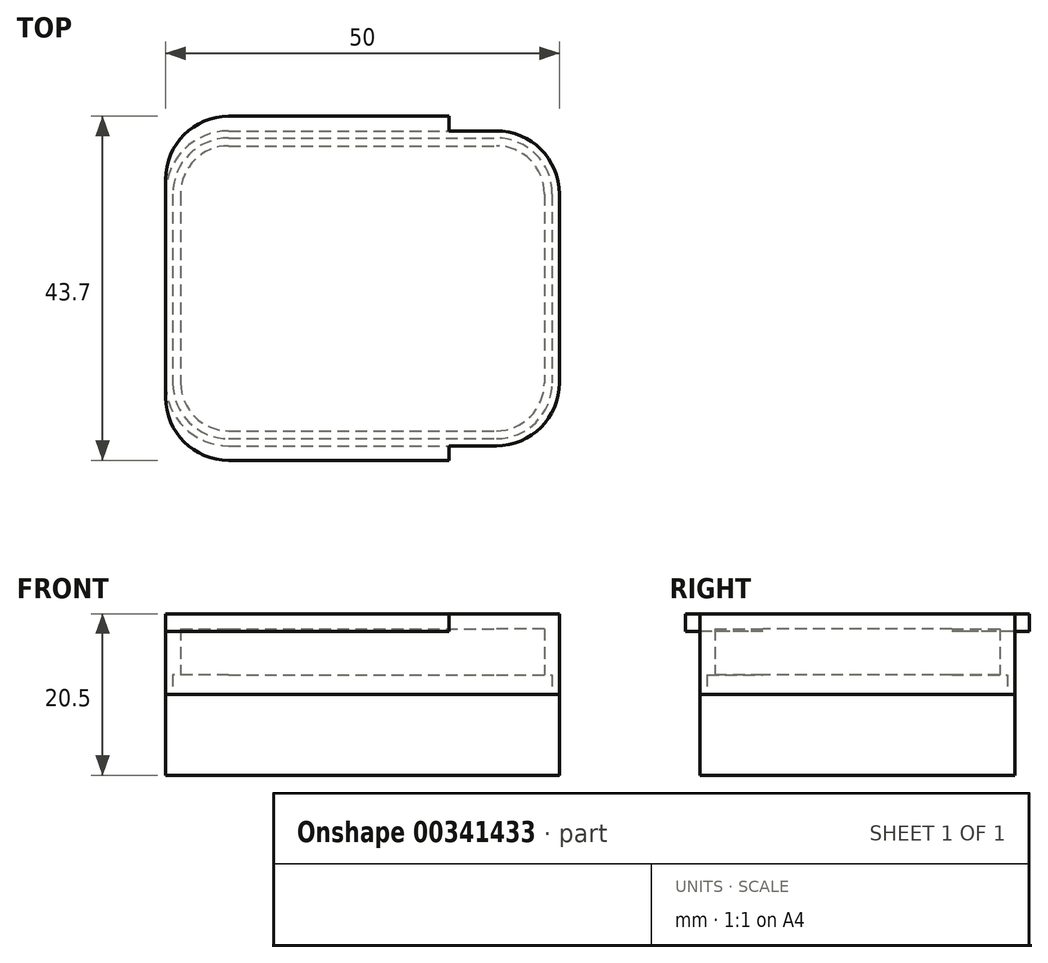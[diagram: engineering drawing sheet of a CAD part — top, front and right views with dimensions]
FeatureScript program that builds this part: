
annotation { "Feature Type Name" : "Feature", "Feature Type Description" : "" }
export const myFeature = defineFeature(function(context is Context, id is Id, definition is map)
    precondition{}
    {
        {
            var Q0;
            Q0=qCreatedBy(makeId("Top.planeOp"),FACE);
            var sketch = newSketch(context, id + "F0", { "sketchPlane" : qUnion([Q0])});
            skLineSegment(sketch, "E0.bottom", {"start": v(-17, 20) * mm, "end": v(17, 20) * mm});
            skLineSegment(sketch, "E0.top", {"start": v(-17, -20) * mm, "end": v(17, -20) * mm});
            skLineSegment(sketch, "E0.left", {"start": v(-25, 12) * mm, "end": v(-25, -12) * mm});
            skLineSegment(sketch, "E0.right", {"start": v(25, 12) * mm, "end": v(25, -12) * mm});
            skPoint(sketch, "E1.visualSharp", {"position": v(25, 20) * mm});
            skArc(sketch, "E1.filletArc", {"start": v(25, 12) * mm, "mid": v(22.66, 17.66) * mm, "end": v(17, 20) * mm});
            skPoint(sketch, "E2.visualSharp", {"position": v(-25, 20) * mm});
            skPoint(sketch, "E3.visualSharp", {"position": v(-25, -20) * mm});
            skArc(sketch, "E3.filletArc", {"start": v(-25, -12) * mm, "mid": v(-22.66, -17.66) * mm, "end": v(-17, -20) * mm});
            skPoint(sketch, "E4.visualSharp", {"position": v(25, -20) * mm});
            skArc(sketch, "E5.filletArc", {"start": v(-17, 20) * mm, "mid": v(-22.66, 17.66) * mm, "end": v(-25, 12) * mm});
            skArc(sketch, "E6.filletArc", {"start": v(17, -20) * mm, "mid": v(22.66, -17.66) * mm, "end": v(25, -12) * mm});
            skSolve(sketch);
        }
        {
            var Q0;
            Q0=makeQuery(id+"F0.imprint","IMPRINT",FACE,{"disambiguationData":[TD([[makeQuery(id+"F0.imprint","IMPRINT",EDGE,{"derivedFrom":sQuery(id+"F0.wireOp",EDGE,"E0.bottom")}),-1.0]])]});
            extrude(context, id + "F1", {"entities" : qUnion([Q0]), "depth" : 10.25 * mm});
        }
        {
            var Q0;
            Q0=makeQuery(id+"F1.opExtrude","CAP_FACE",FACE,{"disambiguationData":[OSD([sQuery(id+"F0.wireOp",EDGE,"E0.bottom"),sQuery(id+"F0.wireOp",EDGE,"E0.top"),sQuery(id+"F0.wireOp",EDGE,"E0.left"),sQuery(id+"F0.wireOp",EDGE,"E0.right"),sQuery(id+"F0.wireOp",EDGE,"E1.filletArc"),sQuery(id+"F0.wireOp",EDGE,"E3.filletArc"),sQuery(id+"F0.wireOp",EDGE,"E5.filletArc"),sQuery(id+"F0.wireOp",EDGE,"E6.filletArc")])],"isStart":false});
            var sketch = newSketch(context, id + "F2", { "sketchPlane" : qUnion([Q0])});
            skLineSegment(sketch, "E7.bottom", {"start": v(-17, 21.85) * mm, "end": v(11, 21.85) * mm});
            skLineSegment(sketch, "E7.top", {"start": v(-17, -21.85) * mm, "end": v(11, -21.85) * mm});
            skLineSegment(sketch, "E7.left", {"start": v(-25, 13.85) * mm, "end": v(-25, -13.85) * mm});
            skLineSegment(sketch, "E7.right", {"start": v(11, 21.85) * mm, "end": v(11, -21.85) * mm});
            skPoint(sketch, "E8.visualSharp", {"position": v(-25, 21.85) * mm});
            skArc(sketch, "E8.filletArc", {"start": v(-17, 21.85) * mm, "mid": v(-22.66, 19.5) * mm, "end": v(-25, 13.85) * mm});
            skPoint(sketch, "E9.visualSharp", {"position": v(-25, -21.85) * mm});
            skArc(sketch, "E9.filletArc", {"start": v(-25, -13.85) * mm, "mid": v(-22.66, -19.5) * mm, "end": v(-17, -21.85) * mm});
            skSolve(sketch);
        }
        {
            var Q0;
            {var subQ4=sQuery(id+"F2.wireOp",EDGE,"E7.bottom");Q0=makeQuery(id+"F2.imprint","IMPRINT",FACE,{"disambiguationData":[TD([[makeQuery(id+"F2.imprint","IMPRINT",EDGE,{"derivedFrom":subQ4}),-1.0]])]});}
            var Q1;
            {var subQ1=sQuery(id+"F2.wireOp",EDGE,"E7.top");Q1=makeQuery(id+"F2.imprint","IMPRINT",FACE,{"disambiguationData":[TD([[makeQuery(id+"F2.imprint","IMPRINT",EDGE,{"derivedFrom":subQ1}),1.0]])]});}
            extrude(context, id + "F3", {"entities" : qUnion([Q0, Q1]), "operationType" : NewBodyOperationType.ADD, "oppositeDirection" : true, "depth" : 2.25 * mm});
        }
        {
            var Q0;
            Q0=makeQuery(id+"F1.opExtrude","CAP_FACE",FACE,{"disambiguationData":[OSD([sQuery(id+"F0.wireOp",EDGE,"E0.bottom"),sQuery(id+"F0.wireOp",EDGE,"E0.top"),sQuery(id+"F0.wireOp",EDGE,"E0.left"),sQuery(id+"F0.wireOp",EDGE,"E0.right"),sQuery(id+"F0.wireOp",EDGE,"E1.filletArc"),sQuery(id+"F0.wireOp",EDGE,"E3.filletArc"),sQuery(id+"F0.wireOp",EDGE,"E5.filletArc"),sQuery(id+"F0.wireOp",EDGE,"E6.filletArc")])],"isStart":true});
            var sketch = newSketch(context, id + "F4", { "sketchPlane" : qUnion([Q0])});
            skArc(sketch, "E10.0.0", {"start": v(-17, 20) * mm, "mid": v(-22.66, 17.66) * mm, "end": v(-25, 12) * mm});
            skLineSegment(sketch, "E10.0.1", {"start": v(-25, 12) * mm, "end": v(-25, -12) * mm});
            skArc(sketch, "E10.0.2", {"start": v(-25, -12) * mm, "mid": v(-22.66, -17.66) * mm, "end": v(-17, -20) * mm});
            skLineSegment(sketch, "E10.0.3", {"start": v(-17, -20) * mm, "end": v(17, -20) * mm});
            skArc(sketch, "E10.0.4", {"start": v(17, -20) * mm, "mid": v(22.66, -17.66) * mm, "end": v(25, -12) * mm});
            skLineSegment(sketch, "E10.0.5", {"start": v(25, -12) * mm, "end": v(25, 12) * mm});
            skArc(sketch, "E10.0.6", {"start": v(25, 12) * mm, "mid": v(22.66, 17.66) * mm, "end": v(17, 20) * mm});
            skLineSegment(sketch, "E10.0.7", {"start": v(17, 20) * mm, "end": v(-17, 20) * mm});
            skSolve(sketch);
        }
        {
            var Q0;
            Q0=makeQuery(id+"F4.imprint","IMPRINT",FACE,{"disambiguationData":[TD([[makeQuery(id+"F4.imprint","IMPRINT",EDGE,{"derivedFrom":sQuery(id+"F4.wireOp",EDGE,"E10.0.0")}),-1.0]])]});
            extrude(context, id + "F5", {"entities" : qUnion([Q0]), "depth" : 10.25 * mm});
        }
        {
            var Q0;
            Q0=makeQuery(id+"F1.opExtrude","CAP_FACE",FACE,{"disambiguationData":[OSD([sQuery(id+"F0.wireOp",EDGE,"E0.bottom"),sQuery(id+"F0.wireOp",EDGE,"E0.top"),sQuery(id+"F0.wireOp",EDGE,"E0.left"),sQuery(id+"F0.wireOp",EDGE,"E0.right"),sQuery(id+"F0.wireOp",EDGE,"E1.filletArc"),sQuery(id+"F0.wireOp",EDGE,"E3.filletArc"),sQuery(id+"F0.wireOp",EDGE,"E5.filletArc"),sQuery(id+"F0.wireOp",EDGE,"E6.filletArc")])],"isStart":true});
            shell(context, id + "F6", {"entities" : qUnion([Q0]), "thickness" : 1.9 * mm});
        }
        {
            var Q0;
            Q0=makeQuery(id+"F1.opExtrude","CAP_FACE",FACE,{"disambiguationData":[OSD([sQuery(id+"F0.wireOp",EDGE,"E0.bottom"),sQuery(id+"F0.wireOp",EDGE,"E0.top"),sQuery(id+"F0.wireOp",EDGE,"E0.left"),sQuery(id+"F0.wireOp",EDGE,"E0.right"),sQuery(id+"F0.wireOp",EDGE,"E1.filletArc"),sQuery(id+"F0.wireOp",EDGE,"E3.filletArc"),sQuery(id+"F0.wireOp",EDGE,"E5.filletArc"),sQuery(id+"F0.wireOp",EDGE,"E6.filletArc")])],"isStart":true});
            var sketch = newSketch(context, id + "F7", { "sketchPlane" : qUnion([Q0])});
            skArc(sketch, "E11.0", {"start": v(-23.1, 12) * mm, "mid": v(-21.31, 16.31) * mm, "end": v(-17, 18.1) * mm});
            skLineSegment(sketch, "E12.0", {"start": v(-23.1, -12) * mm, "end": v(-23.1, 12) * mm});
            skArc(sketch, "E13.0", {"start": v(-17, -18.1) * mm, "mid": v(-21.31, -16.31) * mm, "end": v(-23.1, -12) * mm});
            skLineSegment(sketch, "E14.0", {"start": v(-17, -18.1) * mm, "end": v(17, -18.1) * mm});
            skArc(sketch, "E15.0", {"start": v(23.1, -12) * mm, "mid": v(21.31, -16.31) * mm, "end": v(17, -18.1) * mm});
            skLineSegment(sketch, "E16.0", {"start": v(23.1, -12) * mm, "end": v(23.1, 12) * mm});
            skPoint(sketch, "E17.0", {"position": v(21.31, 16.31) * mm});
            skArc(sketch, "E18.0", {"start": v(17, 18.1) * mm, "mid": v(21.31, 16.31) * mm, "end": v(23.1, 12) * mm});
            skLineSegment(sketch, "E19.0", {"start": v(-17, 18.1) * mm, "end": v(17, 18.1) * mm});
            skArc(sketch, "E20.0", {"start": v(-24.1, 12) * mm, "mid": v(-22.02, 17.02) * mm, "end": v(-17, 19.1) * mm});
            skLineSegment(sketch, "E20.1", {"start": v(-24.1, -12) * mm, "end": v(-24.1, 12) * mm});
            skLineSegment(sketch, "E20.2", {"start": v(-17, 19.1) * mm, "end": v(17, 19.1) * mm});
            skArc(sketch, "E20.3", {"start": v(-17, -19.1) * mm, "mid": v(-22.02, -17.02) * mm, "end": v(-24.1, -12) * mm});
            skArc(sketch, "E20.4", {"start": v(17, 19.1) * mm, "mid": v(22.02, 17.02) * mm, "end": v(24.1, 12) * mm});
            skLineSegment(sketch, "E20.5", {"start": v(24.1, -12) * mm, "end": v(24.1, 12) * mm});
            skArc(sketch, "E20.6", {"start": v(24.1, -12) * mm, "mid": v(22.02, -17.02) * mm, "end": v(17, -19.1) * mm});
            skLineSegment(sketch, "E20.7", {"start": v(-17, -19.1) * mm, "end": v(17, -19.1) * mm});
            skSolve(sketch);
        }
        {
            var Q0;
            Q0=makeQuery(id+"F7.imprint","IMPRINT",FACE,{"disambiguationData":[TD([[makeQuery(id+"F7.imprint","IMPRINT",EDGE,{"derivedFrom":sQuery(id+"F7.wireOp",EDGE,"E11.0")}),1.0]])]});
            extrude(context, id + "F8", {"entities" : qUnion([Q0]), "operationType" : NewBodyOperationType.REMOVE, "oppositeDirection" : true, "depth" : 2.5 * mm});
        }
    });
